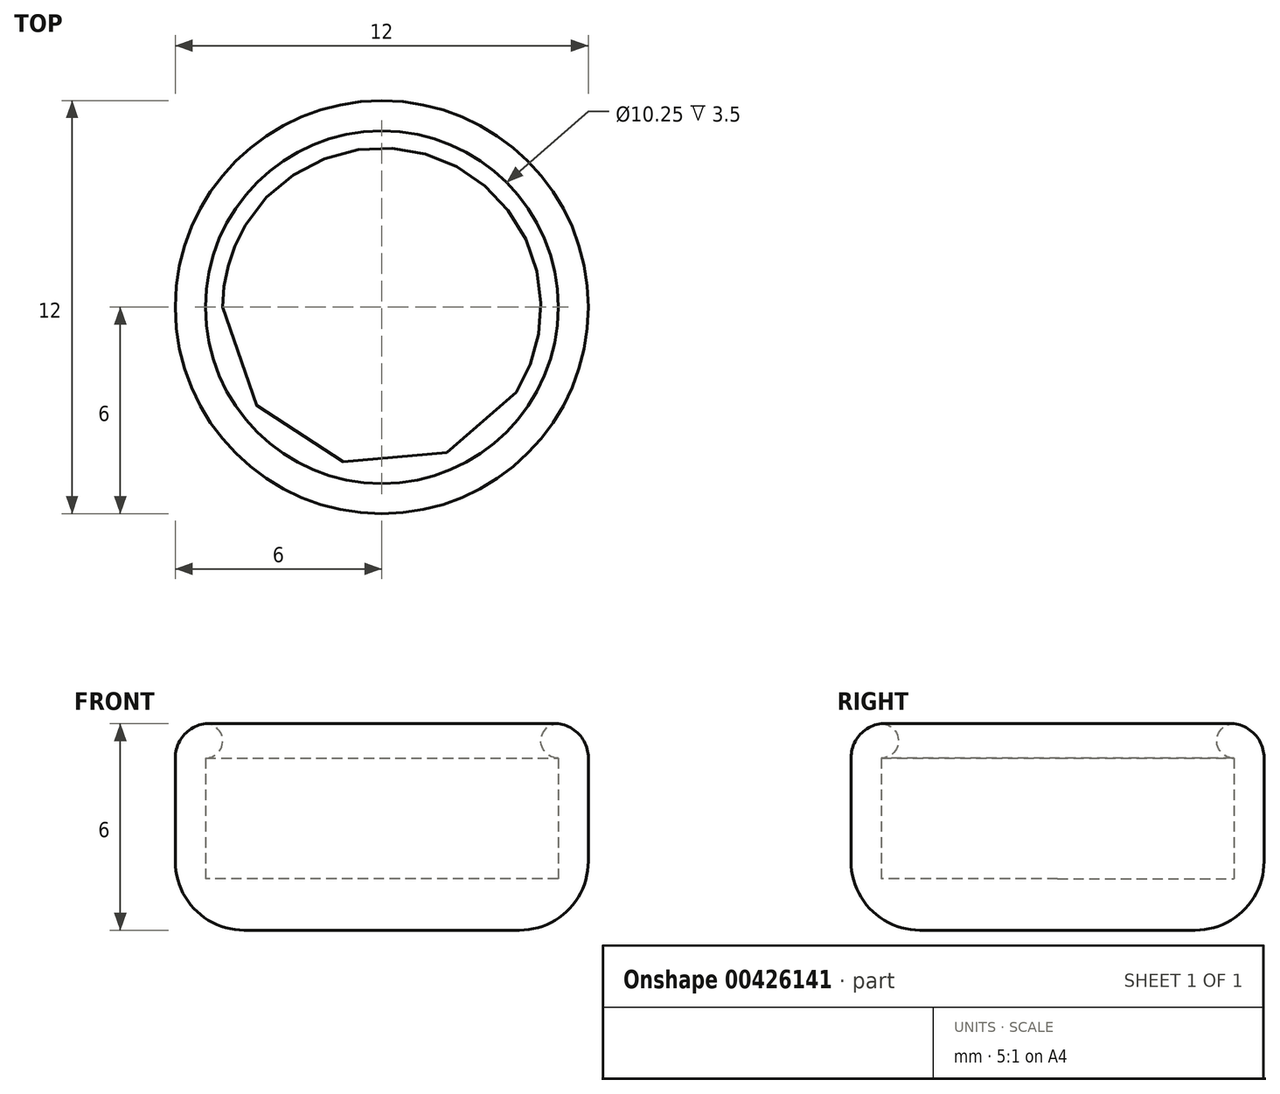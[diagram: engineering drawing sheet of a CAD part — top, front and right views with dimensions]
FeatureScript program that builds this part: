
annotation { "Feature Type Name" : "Feature", "Feature Type Description" : "" }
export const myFeature = defineFeature(function(context is Context, id is Id, definition is map)
    precondition{}
    {
        {
            var Q0;
            Q0=qCreatedBy(makeId("Top.planeOp"),FACE);
            var sketch = newSketch(context, id + "F0", { "sketchPlane" : qUnion([Q0])});
            skCircle(sketch, "E0", {"center": v(0, 0) * mm, "radius": 5.12 * mm});
            skCircle(sketch, "E1", {"center": v(0, 0) * mm, "radius": 6 * mm});
            skSolve(sketch);
        }
        {
            var Q0;
            Q0=makeQuery(id+"F0.imprint","IMPRINT",FACE,{"disambiguationData":[TD([[makeQuery(id+"F0.imprint","IMPRINT",EDGE,{"derivedFrom":sQuery(id+"F0.wireOp",EDGE,"E0")}),1.0]])]});
            extrude(context, id + "F1", {"entities" : qUnion([Q0]), "depth" : 1.5 * mm, "offsetDistance" : 25 * mm});
        }
        {
            var Q0;
            Q0=makeQuery(id+"F0.imprint","IMPRINT",FACE,{"disambiguationData":[TD([[makeQuery(id+"F0.imprint","IMPRINT",EDGE,{"derivedFrom":sQuery(id+"F0.wireOp",EDGE,"E0")}),-1.0]])]});
            extrude(context, id + "F2", {"entities" : qUnion([Q0]), "operationType" : NewBodyOperationType.ADD, "depth" : 6 * mm, "offsetDistance" : 25 * mm});
        }
        {
            var Q0;
            Q0=makeQuery(id+"F2.opExtrude","CAP_EDGE",EDGE,{"disambiguationData":[OSD([sQuery(id+"F0.wireOp",EDGE,"E1")])],"isStart":true});
            fillet(context, id + "F3", {"entities" : qUnion([Q0]), "radius" : 2 * mm, "tangentPropagation" : true, "allowEdgeOverflow" : false});
        }
        {
            var Q0;
            Q0=qCreatedBy(makeId("Right.planeOp"),FACE);
            var sketch = newSketch(context, id + "F4", { "sketchPlane" : qUnion([Q0])});
            skArc(sketch, "E2", {"start": v(-5.12, 5) * mm, "mid": v(-4.63, 5.5) * mm, "end": v(-5.12, 6) * mm});
            skLineSegment(sketch, "E3", {"start": v(-5.12, 6) * mm, "end": v(-5.12, 5) * mm});
            skSolve(sketch);
        }
        {
            var Q0;
            Q0=makeQuery(id+"F4.imprint","IMPRINT",FACE,{"disambiguationData":[TD([[makeQuery(id+"F4.imprint","IMPRINT",EDGE,{"derivedFrom":sQuery(id+"F4.wireOp",EDGE,"E2")}),1.0]])]});
            var Q1;
            Q1=makeQuery(id+"F2.opExtrude","CAP_EDGE",EDGE,{"disambiguationData":[OSD([sQuery(id+"F0.wireOp",EDGE,"E0")])],"isStart":false});
            revolve(context, id + "F5", {"operationType" : NewBodyOperationType.ADD, "surfaceOperationType" : NewSurfaceOperationType.NEW, "entities" : qUnion([Q0]), "axis" : qUnion([Q1]), "revolveType" : RevolveType.FULL});
        }
        {
            var Q0;
            Q0=makeQuery(id+"F2.opExtrude","CAP_EDGE",EDGE,{"disambiguationData":[OSD([sQuery(id+"F0.wireOp",EDGE,"E1")])],"isStart":false});
            var Q1;
            Q1=makeQuery(id+"F1.opExtrude","CAP_EDGE",EDGE,{"disambiguationData":[OSD([sQuery(id+"F0.wireOp",EDGE,"E0")])],"isStart":false});
            fillet(context, id + "F6", {"entities" : qUnion([Q0, Q1]), "radius" : 1 * mm, "tangentPropagation" : true, "allowEdgeOverflow" : false});
        }
    });
